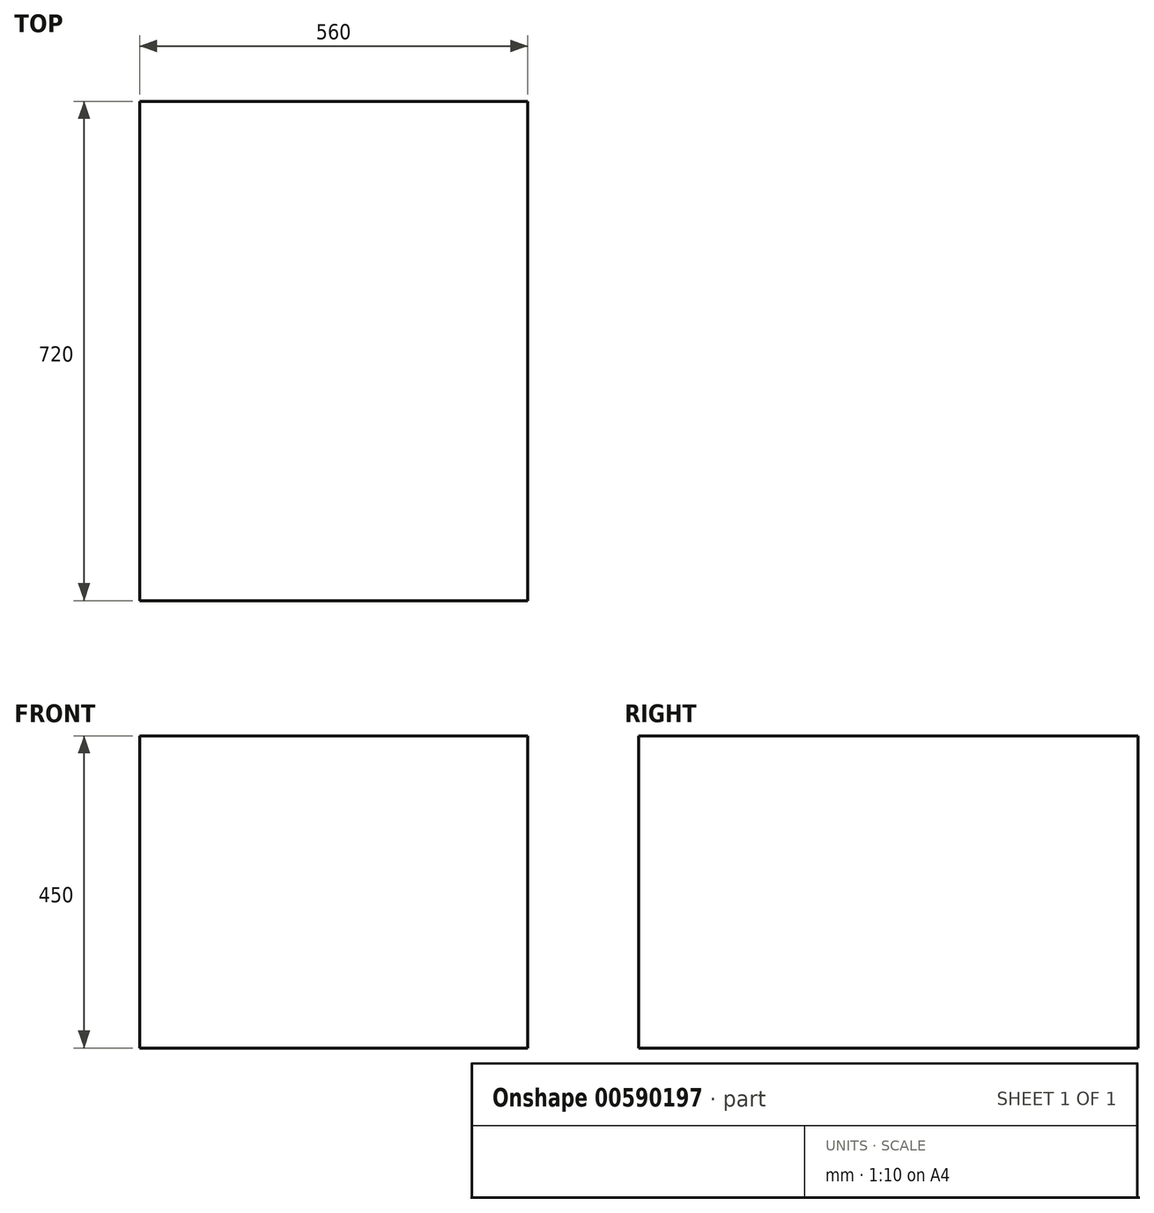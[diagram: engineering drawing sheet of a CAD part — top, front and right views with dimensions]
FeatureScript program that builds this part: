
annotation { "Feature Type Name" : "Feature", "Feature Type Description" : "" }
export const myFeature = defineFeature(function(context is Context, id is Id, definition is map)
    precondition{}
    {
        {
            var Q0;
            Q0=qCreatedBy(makeId("Top.planeOp"),FACE);
            var sketch = newSketch(context, id + "F0", { "sketchPlane" : qUnion([Q0])});
            skLineSegment(sketch, "E0.bottom", {"start": v(0, 0) * mm, "end": v(-560, 0) * mm});
            skLineSegment(sketch, "E0.top", {"start": v(0, -720) * mm, "end": v(-560, -720) * mm});
            skLineSegment(sketch, "E0.left", {"start": v(0, 0) * mm, "end": v(0, -720) * mm});
            skLineSegment(sketch, "E0.right", {"start": v(-560, 0) * mm, "end": v(-560, -720) * mm});
            skSolve(sketch);
        }
        {
            var Q0;
            Q0 = qSketchRegion(id + "F0", true);
            extrude(context, id + "F1", {"entities" : qUnion([Q0]), "depth" : 450 * mm, "offsetDistance" : 25 * mm});
        }
    });
